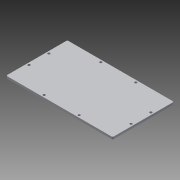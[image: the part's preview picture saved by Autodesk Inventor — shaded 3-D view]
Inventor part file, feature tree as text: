
AUTODESK INVENTOR PART (.ipt)
format: ipt  version: 2015 (Build 190159000, 159)  size: 93,696 bytes
history: native  units: in
note: dims shown in document units (in); Inventor stores cm internally (conversion verified against a paired STEP export)
features: reference x8, extrude x2, sketch x2, fillet x1
ambient origin geometry x8: Origin, YZ Plane, XZ Plane, XY Plane, X Axis, Y Axis, Z Axis, Center Point
bodies: Solid1 (feature_tree)
feature tree (13):
  extrude  "Extrusion1"  Depth=6.75in
  extrude  "Extrusion2"  Depth=0.125in TaperAngle=0.0deg
  fillet  "Fillet1"  Radius=0.125in
  sketch  "Sketch1"  dims[d0=11.75in d1=6.75in]
  sketch  "Sketch3"  dims[d2=0.25in d3=0.0in d25=0.375in d26=0.0in d27=0.125in]
  reference  "Reference1"
  reference  "Reference2"
  reference  "Reference3"
  reference  "Reference4"
  reference  "Reference5"
  reference  "Reference6"
  reference  "Reference7"
  reference  "Reference8"
